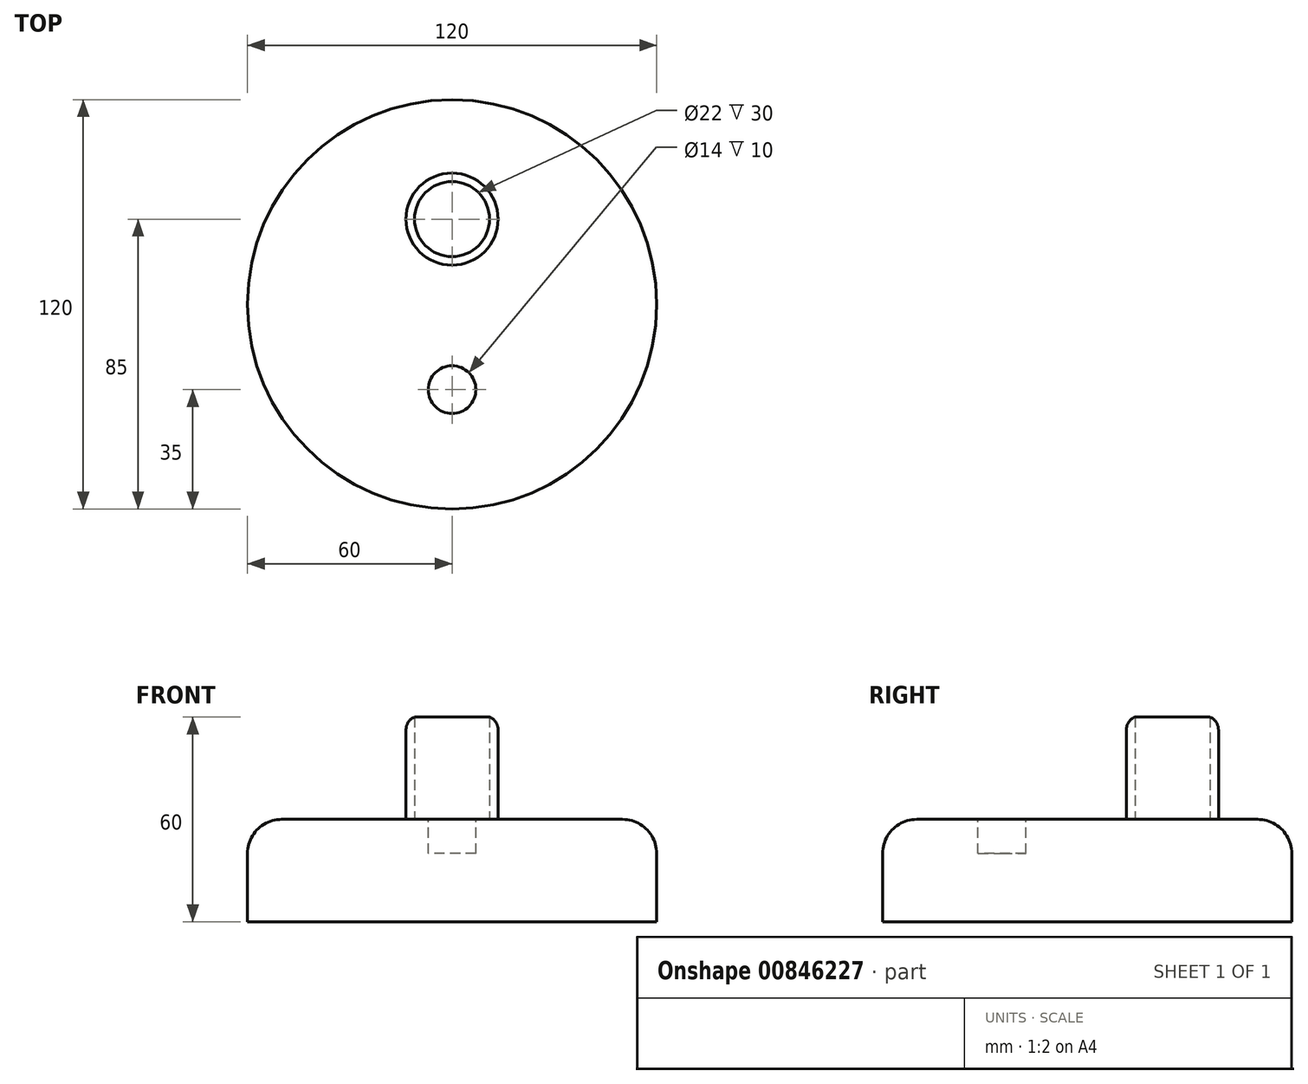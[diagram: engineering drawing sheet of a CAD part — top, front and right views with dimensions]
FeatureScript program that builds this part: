
annotation { "Feature Type Name" : "Feature", "Feature Type Description" : "" }
export const myFeature = defineFeature(function(context is Context, id is Id, definition is map)
    precondition{}
    {
        {
            var Q0;
            Q0=qCreatedBy(makeId("Front.planeOp"),FACE);
            var sketch = newSketch(context, id + "F0", { "sketchPlane" : qUnion([Q0])});
            skLineSegment(sketch, "E0.bottom", {"start": v(0, 0) * mm, "end": v(60, 0) * mm});
            skLineSegment(sketch, "E0.top", {"start": v(0, 30) * mm, "end": v(50, 30) * mm});
            skLineSegment(sketch, "E0.left", {"start": v(0, 0) * mm, "end": v(0, 30) * mm});
            skLineSegment(sketch, "E0.right", {"start": v(60, 0) * mm, "end": v(60, 20) * mm});
            skPoint(sketch, "E1.visualSharp", {"position": v(60, 30) * mm});
            skArc(sketch, "E1.filletArc", {"start": v(60, 20) * mm, "mid": v(57.07, 27.07) * mm, "end": v(50, 30) * mm});
            skSolve(sketch);
        }
        {
            var Q0;
            Q0=makeQuery(id+"F0.imprint","IMPRINT",FACE,{"disambiguationData":[TD([[makeQuery(id+"F0.imprint","IMPRINT",EDGE,{"derivedFrom":sQuery(id+"F0.wireOp",EDGE,"E0.bottom")}),1.0]])]});
            var Q1;
            Q1=sQuery(id+"F0.wireOp",EDGE,"E0.left");
            revolve(context, id + "F1", {"surfaceOperationType" : NewSurfaceOperationType.NEW, "entities" : qUnion([Q0]), "axis" : qUnion([Q1]), "revolveType" : RevolveType.FULL});
        }
        {
            var Q0;
            Q0=makeQuery(id+"F1.opRevolve","SWEPT_FACE",FACE,{"disambiguationData":[OSD([sQuery(id+"F0.wireOp",EDGE,"E0.top")])]});
            var sketch = newSketch(context, id + "F2", { "sketchPlane" : qUnion([Q0])});
            skCircle(sketch, "E2", {"center": v(0, 25) * mm, "radius": 13.5 * mm});
            skCircle(sketch, "E3", {"center": v(0, 25) * mm, "radius": 11 * mm});
            skSolve(sketch);
        }
        {
            var Q0;
            Q0 = qSketchRegion(id + "F2", true);
            extrude(context, id + "F3", {"entities" : qUnion([Q0]), "operationType" : NewBodyOperationType.ADD, "depth" : 30 * mm, "offsetDistance" : 25 * mm});
        }
        {
            var Q0;
            Q0=makeQuery(id+"F3.opExtrude","CAP_EDGE",EDGE,{"disambiguationData":[OSD([sQuery(id+"F2.wireOp",EDGE,"E2")])],"isStart":false});
            fillet(context, id + "F4", {"entities" : qUnion([Q0]), "radius" : 4 * mm, "tangentPropagation" : true, "allowEdgeOverflow" : false});
        }
        {
            var Q0;
            Q0=makeQuery(id+"F3.boolean.opBoolean","SPLIT",FACE,{"disambiguationData":[TD([makeQuery(id+"F1.opRevolve","SWEPT_FACE",FACE,{"disambiguationData":[OSD([sQuery(id+"F0.wireOp",EDGE,"E1.filletArc")])]})])],"derivedFrom":makeQuery(id+"F1.opRevolve","SWEPT_FACE",FACE,{"disambiguationData":[OSD([sQuery(id+"F0.wireOp",EDGE,"E0.top")])]})});
            var sketch = newSketch(context, id + "F5", { "sketchPlane" : qUnion([Q0])});
            skCircle(sketch, "E4", {"center": v(0, -25) * mm, "radius": 7 * mm});
            skSolve(sketch);
        }
        {
            var Q0;
            Q0 = qSketchRegion(id + "F5", true);
            extrude(context, id + "F6", {"entities" : qUnion([Q0]), "operationType" : NewBodyOperationType.REMOVE, "oppositeDirection" : true, "depth" : 10 * mm, "offsetDistance" : 25 * mm});
        }
    });
